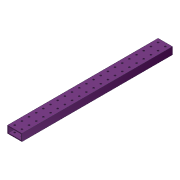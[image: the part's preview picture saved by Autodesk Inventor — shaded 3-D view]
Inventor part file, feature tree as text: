
AUTODESK INVENTOR PART (.ipt)
format: ipt  version: 2012 (Build 160160000, 160)  size: 159,744 bytes
history: native  units: in
note: dims shown in document units (in); Inventor stores cm internally (conversion verified against a paired STEP export)
features: extrude x2, sketch x2, pattern_linear x1
ambient origin geometry x8: Origin, YZ Plane, XZ Plane, XY Plane, X Axis, Y Axis, Z Axis, Center Point
bodies: Solid1 (feature_tree)
feature tree (5):
  extrude  "Extrusion1"  Depth=2.0in
  extrude  "Extrusion2"  Depth=0.125in
  pattern_linear  "Rectangular Pattern1"  Spacing1=0.125in  [1 undecoded]
  sketch  "Sketch1"  dims[d0=1.0in d1=2.0in]
  sketch  "Sketch2"  dims[d2=0.125in d3=0.125in d4=0.125in d5=0.125in d6=21.0in d7=0.0in d8=0.25in d9=0.5in d10=0.5in d11=22.0in d12=0.0in d13=8.2677in d15=1.0in d16=0.7874in d18=1.0in]
note: 1 required parameter value undecoded (feature->parameter linkage not recoverable at this tier; creation-order binding heuristic only, values carry confidence <= 0.55)
